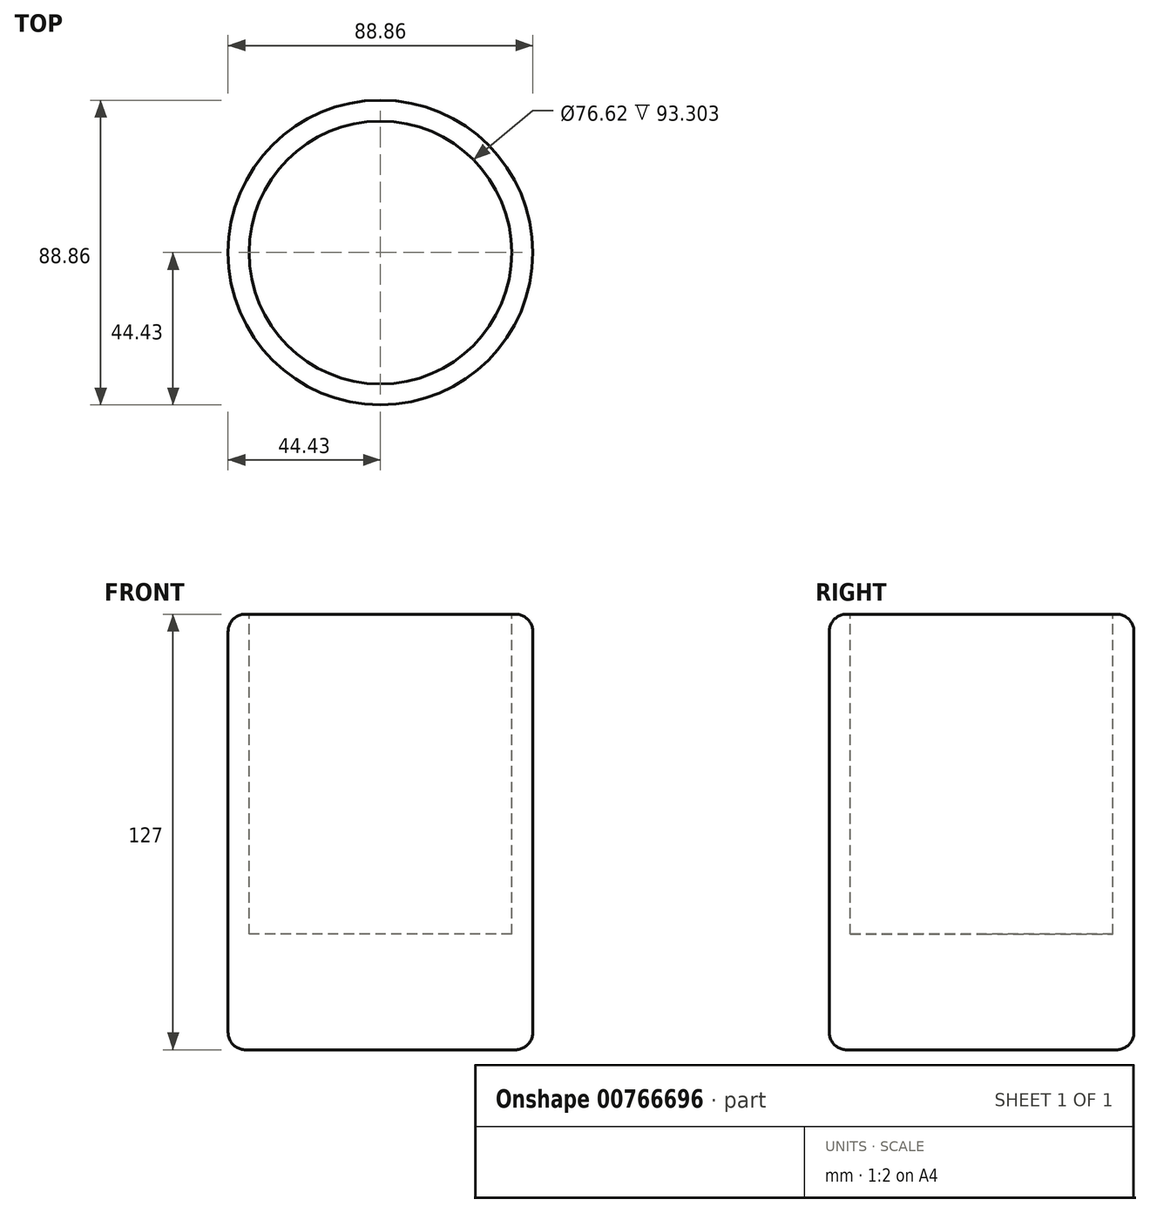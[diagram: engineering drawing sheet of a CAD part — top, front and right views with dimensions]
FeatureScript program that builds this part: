
annotation { "Feature Type Name" : "Feature", "Feature Type Description" : "" }
export const myFeature = defineFeature(function(context is Context, id is Id, definition is map)
    precondition{}
    {
        {
            var Q0;
            Q0=qCreatedBy(makeId("Top.planeOp"),FACE);
            var sketch = newSketch(context, id + "F0", { "sketchPlane" : qUnion([Q0])});
            skCircle(sketch, "E0", {"center": v(0, 0) * mm, "radius": 44.43 * mm});
            skSolve(sketch);
        }
        {
            var Q0;
            Q0=makeQuery(id+"F0.imprint","IMPRINT",FACE,{"disambiguationData":[TD([[makeQuery(id+"F0.imprint","IMPRINT",EDGE,{"derivedFrom":sQuery(id+"F0.wireOp",EDGE,"E0")}),1.0]])]});
            extrude(context, id + "F1", {"entities" : qUnion([Q0]), "depth" : 127 * mm, "offsetDistance" : 25.4 * mm});
        }
        {
            var Q0;
            Q0=makeQuery(id+"F1.opExtrude","CAP_FACE",FACE,{"disambiguationData":[OSD([sQuery(id+"F0.wireOp",EDGE,"E0")])],"isStart":false});
            var sketch = newSketch(context, id + "F2", { "sketchPlane" : qUnion([Q0])});
            skCircle(sketch, "E1", {"center": v(0, 0) * mm, "radius": 38.31 * mm});
            skSolve(sketch);
        }
        {
            var Q0;
            Q0 = qSketchRegion(id + "F2", true);
            extrude(context, id + "F3", {"entities" : qUnion([Q0]), "operationType" : NewBodyOperationType.REMOVE, "oppositeDirection" : true, "depth" : 93.3 * mm, "offsetDistance" : 25.4 * mm});
        }
        {
            var Q0;
            Q0=makeQuery(id+"F1.opExtrude","CAP_EDGE",EDGE,{"disambiguationData":[OSD([sQuery(id+"F0.wireOp",EDGE,"E0")])],"isStart":false});
            fillet(context, id + "F4", {"entities" : qUnion([Q0]), "radius" : 5.08 * mm, "tangentPropagation" : true, "allowEdgeOverflow" : false});
        }
        {
            var Q0;
            Q0=makeQuery(id+"F1.opExtrude","CAP_EDGE",EDGE,{"disambiguationData":[OSD([sQuery(id+"F0.wireOp",EDGE,"E0")])],"isStart":true});
            fillet(context, id + "F5", {"entities" : qUnion([Q0]), "radius" : 5.08 * mm, "tangentPropagation" : true, "allowEdgeOverflow" : false});
        }
    });
